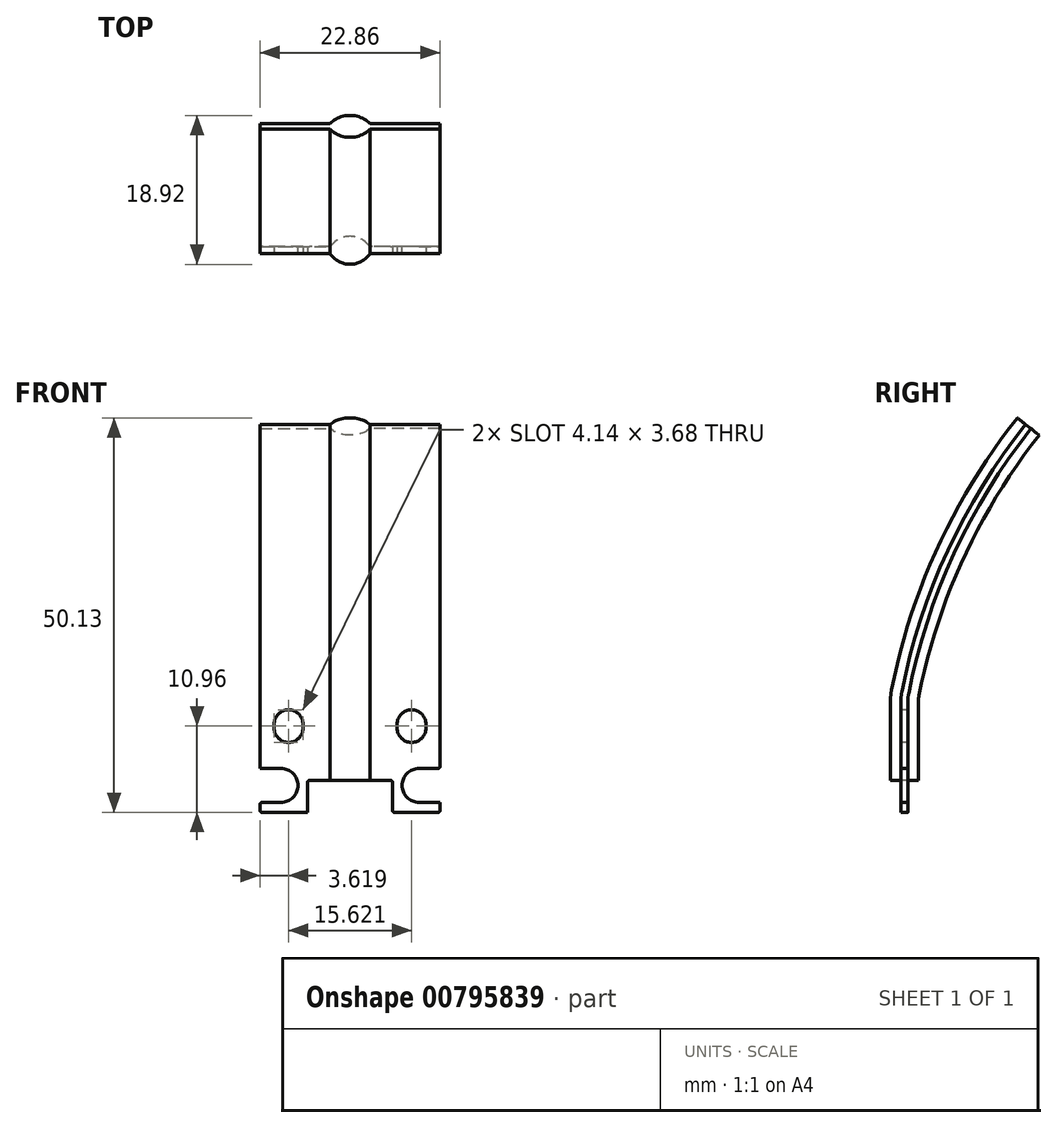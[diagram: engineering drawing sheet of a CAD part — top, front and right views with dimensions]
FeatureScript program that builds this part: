
annotation { "Feature Type Name" : "Feature", "Feature Type Description" : "" }
export const myFeature = defineFeature(function(context is Context, id is Id, definition is map)
    precondition{}
    {
        {
            var Q0;
            Q0=qCreatedBy(makeId("Top.planeOp"),FACE);
            var sketch = newSketch(context, id + "F0", { "sketchPlane" : qUnion([Q0])});
            skLineSegment(sketch, "E0.bottom", {"start": v(-11.43, 0.44) * mm, "end": v(11.43, 0.44) * mm, "construction": true});
            skLineSegment(sketch, "E0.top", {"start": v(-11.43, -0.44) * mm, "end": v(11.43, -0.44) * mm, "construction": true});
            skLineSegment(sketch, "E0.left", {"start": v(-11.43, 0.44) * mm, "end": v(-11.43, -0.44) * mm});
            skLineSegment(sketch, "E0.right", {"start": v(11.43, 0.44) * mm, "end": v(11.43, -0.44) * mm});
            skCircle(sketch, "E1", {"center": v(0, 1.25) * mm, "radius": 3.03 * mm, "construction": true});
            skCircle(sketch, "E2", {"center": v(0, -1.25) * mm, "radius": 3.03 * mm, "construction": true});
            skPoint(sketch, "E2.centerSnap0", {"position": v(0, 0.44) * mm});
            skLineSegment(sketch, "E3", {"start": v(2.92, 0.44) * mm, "end": v(2.92, 11.08) * mm, "construction": true});
            skLineSegment(sketch, "E4", {"start": v(0, -1.78) * mm, "end": v(8.1, -1.78) * mm});
            skArc(sketch, "E5", {"start": v(-2.51, -0.44) * mm, "mid": v(0, -1.78) * mm, "end": v(2.51, -0.44) * mm});
            skArc(sketch, "E6", {"start": v(2.51, 0.44) * mm, "mid": v(0, 1.78) * mm, "end": v(-2.51, 0.44) * mm});
            skLineSegment(sketch, "E7", {"start": v(-11.43, 0.44) * mm, "end": v(-2.51, 0.44) * mm});
            skLineSegment(sketch, "E8", {"start": v(-11.43, -0.44) * mm, "end": v(-2.51, -0.44) * mm});
            skLineSegment(sketch, "E9", {"start": v(2.51, -0.44) * mm, "end": v(11.43, -0.44) * mm});
            skLineSegment(sketch, "E10", {"start": v(11.43, 0.44) * mm, "end": v(2.51, 0.44) * mm});
            skSolve(sketch);
        }
        {
            var Q0;
            Q0=qCreatedBy(makeId("Right.planeOp"),FACE);
            var sketch = newSketch(context, id + "F1", { "sketchPlane" : qUnion([Q0])});
            skLineSegment(sketch, "E11", {"start": v(0, 0) * mm, "end": v(0, 14) * mm});
            skArc(sketch, "E12", {"start": v(15.75, 49.02) * mm, "mid": v(5.9, 33.06) * mm, "end": v(0.12, 15.23) * mm});
            skPoint(sketch, "E13.visualSharp", {"position": v(0, 14.6) * mm});
            skArc(sketch, "E13.filletArc", {"start": v(0.12, 15.23) * mm, "mid": v(0.03, 14.62) * mm, "end": v(0, 14) * mm});
            skSolve(sketch);
        }
        {
            var Q0;
            Q0=makeQuery(id+"F0.imprint","IMPRINT",FACE,{"disambiguationData":[TD([[makeQuery(id+"F0.imprint","IMPRINT",EDGE,{"derivedFrom":sQuery(id+"F0.wireOp",EDGE,"E0.left")}),1.0]])]});
            var Q1;
            Q1 = qConstructionFilter(qBodyType(qCreatedBy(id + "F1" ,EDGE), BodyType.WIRE), ConstructionObject.NO);
            sweep(context, id + "F2", {"profiles" : qUnion([Q0]), "path" : qUnion([Q1])});
        }
        {
            var Q0;
            Q0=qCreatedBy(makeId("Front.planeOp"),FACE);
            var sketch = newSketch(context, id + "F3", { "sketchPlane" : qUnion([Q0])});
            skCircle(sketch, "E14", {"center": v(7.81, 11.19) * mm, "radius": 1.84 * mm, "construction": true});
            skCircle(sketch, "E15", {"center": v(7.81, 10.73) * mm, "radius": 1.84 * mm, "construction": true});
            skLineSegment(sketch, "E16", {"start": v(5.97, 11.19) * mm, "end": v(5.97, 10.73) * mm});
            skLineSegment(sketch, "E17", {"start": v(9.65, 11.19) * mm, "end": v(9.65, 10.73) * mm});
            skArc(sketch, "E18", {"start": v(5.97, 10.73) * mm, "mid": v(7.81, 8.9) * mm, "end": v(9.65, 10.73) * mm});
            skArc(sketch, "E19", {"start": v(9.65, 11.19) * mm, "mid": v(7.81, 13.03) * mm, "end": v(5.97, 11.19) * mm});
            skLineSegment(sketch, "E20.MirrorCS", {"start": v(-5.97, 11.19) * mm, "end": v(-5.97, 10.73) * mm});
            skCircle(sketch, "E21.MirrorC", {"center": v(-7.81, 11.19) * mm, "radius": 1.84 * mm, "construction": true});
            skLineSegment(sketch, "E22.MirrorCS", {"start": v(-9.65, 11.19) * mm, "end": v(-9.65, 10.73) * mm});
            skCircle(sketch, "E23.MirrorC", {"center": v(-7.81, 10.73) * mm, "radius": 1.84 * mm, "construction": true});
            skArc(sketch, "E24.MirrorCS", {"start": v(-9.65, 11.19) * mm, "mid": v(-7.81, 13.03) * mm, "end": v(-5.97, 11.19) * mm});
            skArc(sketch, "E25.MirrorCS", {"start": v(-5.97, 10.73) * mm, "mid": v(-7.81, 8.9) * mm, "end": v(-9.65, 10.73) * mm});
            skSolve(sketch);
        }
        {
            var Q0;
            Q0 = qSketchRegion(id + "F3", true);
            extrude(context, id + "F4", {"entities" : qUnion([Q0]), "operationType" : NewBodyOperationType.REMOVE, "endBound" : BoundingType.SYMMETRIC, "oppositeDirection" : true, "depth" : 25.4 * mm, "offsetDistance" : 25.4 * mm});
        }
        {
            var Q0;
            Q0=qCreatedBy(makeId("Front.planeOp"),FACE);
            var sketch = newSketch(context, id + "F5", { "sketchPlane" : qUnion([Q0])});
            skCircle(sketch, "E26", {"center": v(8.76, 3.43) * mm, "radius": 2.16 * mm, "construction": true});
            skLineSegment(sketch, "E27", {"start": v(8.76, 1.27) * mm, "end": v(11.43, 1.27) * mm});
            skLineSegment(sketch, "E28", {"start": v(8.76, 5.59) * mm, "end": v(11.43, 5.59) * mm});
            skLineSegment(sketch, "E29", {"start": v(6.6, 3.43) * mm, "end": v(6.6, 0) * mm, "construction": true});
            skArc(sketch, "E30", {"start": v(8.76, 5.59) * mm, "mid": v(6.6, 3.43) * mm, "end": v(8.76, 1.27) * mm});
            skLineSegment(sketch, "E31", {"start": v(11.43, 5.59) * mm, "end": v(11.43, 1.27) * mm});
            skArc(sketch, "E32.MirrorCS", {"start": v(-8.76, 5.59) * mm, "mid": v(-6.6, 3.43) * mm, "end": v(-8.76, 1.27) * mm});
            skCircle(sketch, "E33.MirrorC", {"center": v(-8.76, 3.43) * mm, "radius": 2.16 * mm, "construction": true});
            skLineSegment(sketch, "E34.MirrorCS", {"start": v(-8.76, 1.27) * mm, "end": v(-11.43, 1.27) * mm});
            skLineSegment(sketch, "E35.MirrorCS", {"start": v(-8.76, 5.59) * mm, "end": v(-11.43, 5.59) * mm});
            skLineSegment(sketch, "E36.MirrorCS", {"start": v(-11.43, 5.59) * mm, "end": v(-11.43, 1.27) * mm});
            skSolve(sketch);
        }
        {
            var Q0;
            Q0 = qSketchRegion(id + "F5", true);
            extrude(context, id + "F6", {"entities" : qUnion([Q0]), "operationType" : NewBodyOperationType.REMOVE, "endBound" : BoundingType.SYMMETRIC, "depth" : 25.4 * mm, "offsetDistance" : 25.4 * mm});
        }
        {
            var Q0;
            Q0=qCreatedBy(makeId("Front.planeOp"),FACE);
            var sketch = newSketch(context, id + "F7", { "sketchPlane" : qUnion([Q0])});
            skLineSegment(sketch, "E37.bottom", {"start": v(-5.4, 4.06) * mm, "end": v(5.4, 4.06) * mm});
            skLineSegment(sketch, "E37.top", {"start": v(-5.4, 0) * mm, "end": v(5.4, 0) * mm});
            skLineSegment(sketch, "E37.left", {"start": v(-5.4, 4.06) * mm, "end": v(-5.4, 0) * mm});
            skLineSegment(sketch, "E37.right", {"start": v(5.4, 4.06) * mm, "end": v(5.4, 0) * mm});
            skSolve(sketch);
        }
        {
            var Q0;
            Q0 = qSketchRegion(id + "F7", true);
            extrude(context, id + "F8", {"entities" : qUnion([Q0]), "operationType" : NewBodyOperationType.REMOVE, "endBound" : BoundingType.SYMMETRIC, "oppositeDirection" : true, "depth" : 25.4 * mm, "offsetDistance" : 25.4 * mm});
        }
        {
            var Q0;
            Q0=makeQuery(id+"F6.boolean.opBoolean","COPY",EDGE,{"derivedFrom":makeQuery(id+"F6.opExtrude","SWEPT_EDGE",EDGE,{"disambiguationData":[OSD([sQuery(id+"F5.wireOp",EDGE,"E28"),sQuery(id+"F5.wireOp",EDGE,"E31")])]})});
            var Q1;
            Q1=makeQuery(id+"F6.boolean.opBoolean","COPY",EDGE,{"derivedFrom":makeQuery(id+"F6.opExtrude","SWEPT_EDGE",EDGE,{"disambiguationData":[OSD([sQuery(id+"F5.wireOp",EDGE,"E27"),sQuery(id+"F5.wireOp",EDGE,"E31")])]})});
            var Q2;
            Q2=makeQuery(id+"F2.opSweep","CAP_EDGE",EDGE,{"disambiguationData":[OSD([sQuery(id+"F0.wireOp",EDGE,"E0.right"),sQuery(id+"F1.wireOp",VERTEX,"E11.start")])],"isStart":true});
            var Q3;
            Q3=makeQuery(id+"F6.boolean.opBoolean","COPY",EDGE,{"derivedFrom":makeQuery(id+"F6.opExtrude","SWEPT_EDGE",EDGE,{"disambiguationData":[OSD([sQuery(id+"F5.wireOp",EDGE,"E35.MirrorCS"),sQuery(id+"F5.wireOp",EDGE,"E36.MirrorCS")])]})});
            var Q4;
            Q4=makeQuery(id+"F6.boolean.opBoolean","COPY",EDGE,{"derivedFrom":makeQuery(id+"F6.opExtrude","SWEPT_EDGE",EDGE,{"disambiguationData":[OSD([sQuery(id+"F5.wireOp",EDGE,"E34.MirrorCS"),sQuery(id+"F5.wireOp",EDGE,"E36.MirrorCS")])]})});
            var Q5;
            Q5=makeQuery(id+"F2.opSweep","CAP_EDGE",EDGE,{"disambiguationData":[OSD([sQuery(id+"F0.wireOp",EDGE,"E0.left"),sQuery(id+"F1.wireOp",VERTEX,"E11.start")])],"isStart":true});
            var Q6;
            Q6=makeQuery(id+"F8.boolean.opBoolean","COPY",EDGE,{"derivedFrom":makeQuery(id+"F8.opExtrude","SWEPT_EDGE",EDGE,{"disambiguationData":[OSD([sQuery(id+"F7.wireOp",EDGE,"E37.top"),sQuery(id+"F7.wireOp",EDGE,"E37.left")])]})});
            var Q7;
            Q7=makeQuery(id+"F8.boolean.opBoolean","COPY",EDGE,{"derivedFrom":makeQuery(id+"F8.opExtrude","SWEPT_EDGE",EDGE,{"disambiguationData":[OSD([sQuery(id+"F7.wireOp",EDGE,"E37.bottom"),sQuery(id+"F7.wireOp",EDGE,"E37.left")])]})});
            var Q8;
            Q8=makeQuery(id+"F8.boolean.opBoolean","COPY",EDGE,{"derivedFrom":makeQuery(id+"F8.opExtrude","SWEPT_EDGE",EDGE,{"disambiguationData":[OSD([sQuery(id+"F7.wireOp",EDGE,"E37.bottom"),sQuery(id+"F7.wireOp",EDGE,"E37.right")])]})});
            var Q9;
            Q9=makeQuery(id+"F8.boolean.opBoolean","COPY",EDGE,{"derivedFrom":makeQuery(id+"F8.opExtrude","SWEPT_EDGE",EDGE,{"disambiguationData":[OSD([sQuery(id+"F7.wireOp",EDGE,"E37.top"),sQuery(id+"F7.wireOp",EDGE,"E37.right")])]})});
            fillet(context, id + "F9", {"entities" : qUnion([Q0, Q1, Q2, Q3, Q4, Q5, Q6, Q7, Q8, Q9]), "radius" : 0.25 * mm, "tangentPropagation" : true, "allowEdgeOverflow" : false});
        }
    });
